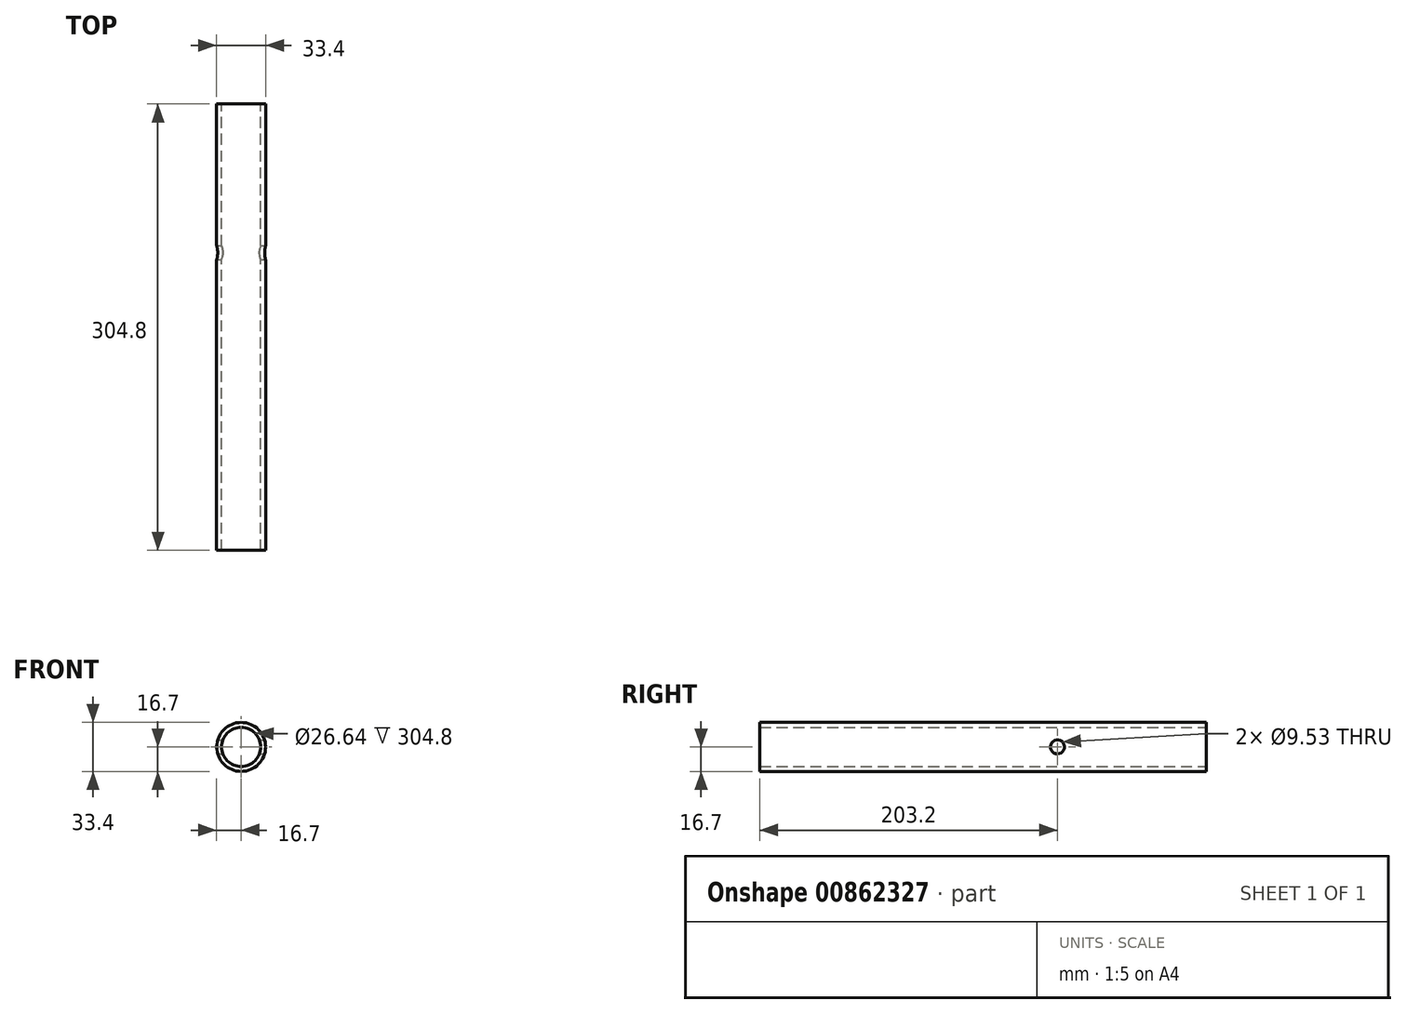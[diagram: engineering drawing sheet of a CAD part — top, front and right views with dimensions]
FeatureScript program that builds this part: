
annotation { "Feature Type Name" : "Feature", "Feature Type Description" : "" }
export const myFeature = defineFeature(function(context is Context, id is Id, definition is map)
    precondition{}
    {
        {
            var Q0;
            Q0=qCreatedBy(makeId("Front.planeOp"),FACE);
            var sketch = newSketch(context, id + "F0", { "sketchPlane" : qUnion([Q0])});
            skCircle(sketch, "E0", {"center": v(0, 0) * mm, "radius": 16.7 * mm});
            skCircle(sketch, "E1", {"center": v(0, 0) * mm, "radius": 13.32 * mm});
            skSolve(sketch);
        }
        {
            var Q0;
            Q0=makeQuery(id+"F0.imprint","IMPRINT",FACE,{"disambiguationData":[TD([[makeQuery(id+"F0.imprint","IMPRINT",EDGE,{"derivedFrom":sQuery(id+"F0.wireOp",EDGE,"E0")}),1.0]])]});
            extrude(context, id + "F1", {"entities" : qUnion([Q0]), "endBound" : BoundingType.SYMMETRIC, "depth" : 304.8 * mm, "offsetDistance" : 25.4 * mm});
        }
        {
            var Q0;
            Q0=qCreatedBy(makeId("Right.planeOp"),FACE);
            var sketch = newSketch(context, id + "F2", { "sketchPlane" : qUnion([Q0])});
            skCircle(sketch, "E2", {"center": v(50.8, 0) * mm, "radius": 4.76 * mm});
            skSolve(sketch);
        }
        {
            var Q0;
            Q0=qSketchRegion(id+"F2",true);
            extrude(context, id + "F3", {"entities" : qUnion([Q0]), "operationType" : NewBodyOperationType.REMOVE, "endBound" : BoundingType.THROUGH_ALL, "oppositeDirection" : true, "depth" : 25.4 * mm, "offsetDistance" : 25.4 * mm, "hasSecondDirection" : true, "secondDirectionBound" : SecondDirectionBoundingType.THROUGH_ALL, "secondDirectionOppositeDirection" : false, "secondDirectionDepth" : 25.4 * mm});
        }
    });
